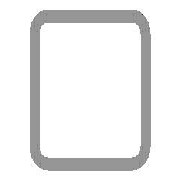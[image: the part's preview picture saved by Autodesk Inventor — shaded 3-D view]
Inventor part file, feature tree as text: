
AUTODESK INVENTOR PART (.ipt)
format: ipt  version: 2025 (Build 290162010, 162A)  size: 130,560 bytes
history: native  units: mm (DEFAULTED — no unit token found)
features: other x4, sketch x1, plane x1
ambient origin geometry x8: Origin, YZ Plane, XZ Plane, XY Plane, X Axis, Y Axis, Z Axis, Center Point
bodies: Solid1 (feature_tree), Body (feature_tree)
feature tree (6):
  parser-record x1  (decoder bookkeeping rows leaked as tree rows — omitted from the tree; the rows remain in map.json)
  other  "Driven Length"
  other  "Start Plane"
  other  "End Plane"
  sketch  "Sketch3"  dims[d3=3000.0mm d4=0.0mm d7=4.0mm d9=40.0mm d11=40.0mm d12=2.0mm d13=-0.0mm d14=3000.0mm d15=20.0mm d16=20.0mm d17=90.0deg d18=3000.0mm]
  plane  "Work Plane3"
